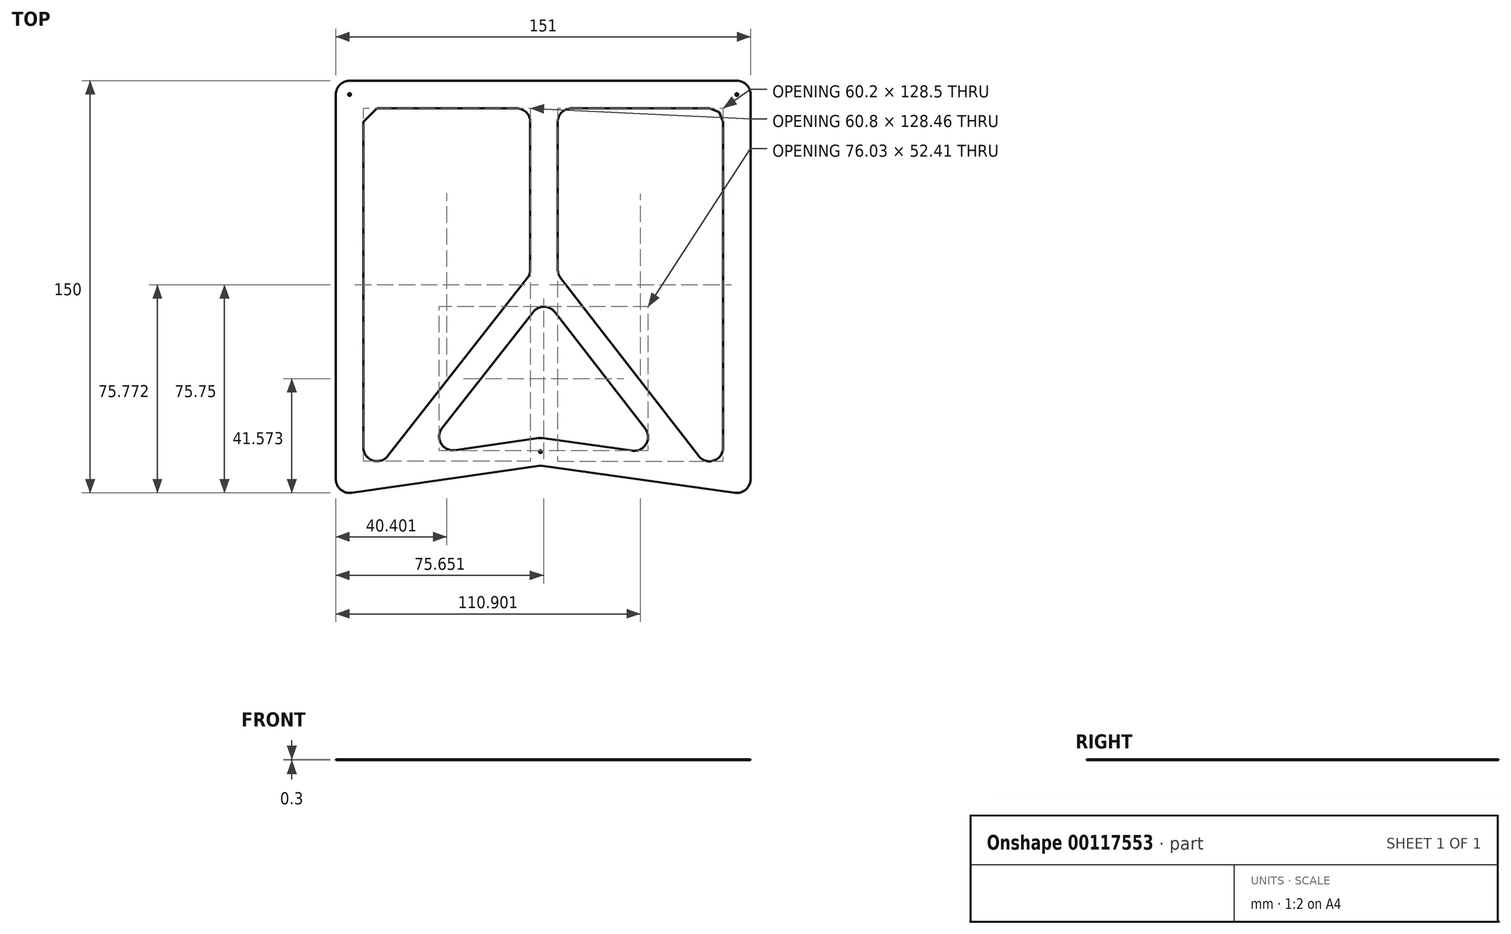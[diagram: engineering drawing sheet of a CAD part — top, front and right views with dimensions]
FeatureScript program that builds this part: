
annotation { "Feature Type Name" : "Feature", "Feature Type Description" : "" }
export const myFeature = defineFeature(function(context is Context, id is Id, definition is map)
    precondition{}
    {
        {
            var Q0;
            Q0=qCreatedBy(makeId("Top.planeOp"),FACE);
            var sketch = newSketch(context, id + "F0", { "sketchPlane" : qUnion([Q0])});
            skLineSegment(sketch, "E0.bottom", {"start": v(-40, 65) * mm, "end": v(40, 65) * mm});
            skLineSegment(sketch, "E0.top", {"start": v(-40, -65) * mm, "end": v(40, -65) * mm});
            skLineSegment(sketch, "E0.left", {"start": v(-40, 65) * mm, "end": v(-40, -65) * mm});
            skLineSegment(sketch, "E0.right", {"start": v(40, 65) * mm, "end": v(40, -65) * mm});
            skLineSegment(sketch, "E1", {"start": v(-40, 0) * mm, "end": v(40, 0) * mm, "construction": true});
            skLineSegment(sketch, "E2.0", {"start": v(-29.6, 64.6) * mm, "end": v(29.6, 64.6) * mm});
            skLineSegment(sketch, "E2.1", {"start": v(-39.6, 54.6) * mm, "end": v(-39.6, -54.6) * mm});
            skLineSegment(sketch, "E2.2", {"start": v(-29.6, -64.6) * mm, "end": v(39.6, -64.6) * mm});
            skLineSegment(sketch, "E2.3", {"start": v(39.6, 54.6) * mm, "end": v(39.6, -64.6) * mm});
            skLineSegment(sketch, "E3.bottom", {"start": v(-15, 25) * mm, "end": v(35, 25) * mm});
            skLineSegment(sketch, "E3.top", {"start": v(-15, -45) * mm, "end": v(35, -45) * mm});
            skLineSegment(sketch, "E3.left", {"start": v(-15, 25) * mm, "end": v(-15, -45) * mm});
            skLineSegment(sketch, "E3.right", {"start": v(35, 25) * mm, "end": v(35, -45) * mm});
            skLineSegment(sketch, "E4.0", {"start": v(-14.6, 24.6) * mm, "end": v(34.6, 24.6) * mm});
            skLineSegment(sketch, "E4.1", {"start": v(-14.6, 24.6) * mm, "end": v(-14.6, -44.6) * mm});
            skLineSegment(sketch, "E4.2", {"start": v(-14.6, -44.6) * mm, "end": v(34.6, -44.6) * mm});
            skLineSegment(sketch, "E4.3", {"start": v(34.6, 24.6) * mm, "end": v(34.6, -44.6) * mm});
            skPoint(sketch, "E5.visualSharp", {"position": v(-39.6, -64.6) * mm});
            skLineSegment(sketch, "E6", {"start": v(29.6, 64.6) * mm, "end": v(34.19, 62.7) * mm});
            skLineSegment(sketch, "E7", {"start": v(39.6, 54.6) * mm, "end": v(37.7, 59.19) * mm});
            skLineSegment(sketch, "E8", {"start": v(29.6, 64.6) * mm, "end": v(39.6, 54.6) * mm, "construction": true});
            skLineSegment(sketch, "E9", {"start": v(39.6, 54.6) * mm, "end": v(39.6, 59.19) * mm, "construction": true});
            skLineSegment(sketch, "E10", {"start": v(39.6, 59.19) * mm, "end": v(37.7, 59.19) * mm, "construction": true});
            skLineSegment(sketch, "E11", {"start": v(37.7, 59.19) * mm, "end": v(36.36, 57.84) * mm, "construction": true});
            skLineSegment(sketch, "E12", {"start": v(-39.6, -54.6) * mm, "end": v(-29.6, -64.6) * mm});
            skLineSegment(sketch, "E13", {"start": v(-39.6, -54.6) * mm, "end": v(-39.6, -64.6) * mm, "construction": true});
            skLineSegment(sketch, "E14", {"start": v(-39.6, -64.6) * mm, "end": v(-29.6, -64.6) * mm, "construction": true});
            skLineSegment(sketch, "E15", {"start": v(-39.6, 54.6) * mm, "end": v(-36.67, 61.67) * mm});
            skLineSegment(sketch, "E16", {"start": v(-36.67, 61.67) * mm, "end": v(-29.6, 64.6) * mm});
            skLineSegment(sketch, "E17", {"start": v(-29.6, 64.6) * mm, "end": v(-39.6, 54.6) * mm, "construction": true});
            skLineSegment(sketch, "E18", {"start": v(-36.67, 64.6) * mm, "end": v(-36.67, 61.67) * mm, "construction": true});
            skLineSegment(sketch, "E19", {"start": v(-36.67, 61.67) * mm, "end": v(-34.6, 59.6) * mm, "construction": true});
            skLineSegment(sketch, "E20", {"start": v(-29.6, 64.6) * mm, "end": v(-39.6, 64.6) * mm, "construction": true});
            skLineSegment(sketch, "E21", {"start": v(-39.6, 64.6) * mm, "end": v(-39.6, 54.6) * mm, "construction": true});
            skLineSegment(sketch, "E22", {"start": v(34.19, 62.7) * mm, "end": v(37.7, 59.19) * mm});
            skSolve(sketch);
        }
        {
            var Q0;
            Q0=qCreatedBy(makeId("Top.planeOp"),FACE);
            var sketch = newSketch(context, id + "F1", { "sketchPlane" : qUnion([Q0])});
            skCircle(sketch, "E23", {"center": v(118.5, 40) * mm, "radius": 0.5 * mm});
            skCircle(sketch, "E24", {"center": v(190, 170) * mm, "radius": 0.5 * mm});
            skCircle(sketch, "E25", {"center": v(49, 170) * mm, "radius": 0.5 * mm});
            skSolve(sketch);
        }
        {
            var Q0;
            Q0 = qSketchRegion(id + "F1", true);
            extrude(context, id + "F2", {"entities" : qUnion([Q0]), "depth" : .3 * mm, "offsetDistance" : 25 * mm});
        }
        {
            var Q0;
            Q0=qCreatedBy(makeId("Top.planeOp"),FACE);
            var sketch = newSketch(context, id + "F3", { "sketchPlane" : qUnion([Q0])});
            skArc(sketch, "E26", {"start": v(119.2, 44.95) * mm, "mid": v(118.5, 45) * mm, "end": v(117.79, 44.95) * mm});
            skArc(sketch, "E27", {"start": v(195, 170) * mm, "mid": v(193.54, 173.54) * mm, "end": v(190, 175) * mm});
            skArc(sketch, "E28", {"start": v(49, 175) * mm, "mid": v(45.46, 173.54) * mm, "end": v(44, 170) * mm});
            skLineSegment(sketch, "E29", {"start": v(44, 170) * mm, "end": v(44, 30) * mm});
            skLineSegment(sketch, "E30", {"start": v(195, 30) * mm, "end": v(195, 170) * mm});
            skLineSegment(sketch, "E31", {"start": v(49, 175) * mm, "end": v(190, 175) * mm});
            skArc(sketch, "E32.filletArc", {"start": v(44, 30) * mm, "mid": v(45.73, 26.22) * mm, "end": v(49.71, 25.05) * mm});
            skArc(sketch, "E33.filletArc", {"start": v(189.3, 25.05) * mm, "mid": v(193.28, 26.23) * mm, "end": v(195, 30) * mm});
            skLineSegment(sketch, "E34.0", {"start": v(59, 165) * mm, "end": v(109.8, 165) * mm});
            skLineSegment(sketch, "E34.1", {"start": v(54, 160) * mm, "end": v(54, 41.54) * mm});
            skLineSegment(sketch, "E34.3", {"start": v(185, 41.5) * mm, "end": v(185, 160) * mm});
            skArc(sketch, "E35.filletArc", {"start": v(59, 165) * mm, "mid": v(55.46, 163.54) * mm, "end": v(54, 160) * mm, "construction": true});
            skArc(sketch, "E36.filletArc", {"start": v(185, 160) * mm, "mid": v(183.54, 163.54) * mm, "end": v(180, 165) * mm, "construction": true});
            skLineSegment(sketch, "E37", {"start": v(87.33, 40.57) * mm, "end": v(117.79, 44.95) * mm});
            skLineSegment(sketch, "E38", {"start": v(151.99, 40.37) * mm, "end": v(119.2, 44.95) * mm});
            skLineSegment(sketch, "E39", {"start": v(49.71, 25.05) * mm, "end": v(118.5, 34.95) * mm});
            skLineSegment(sketch, "E40", {"start": v(189.3, 25.05) * mm, "end": v(118.5, 34.95) * mm});
            skLineSegment(sketch, "E41", {"start": v(82.68, 39.9) * mm, "end": v(84.1, 30) * mm, "construction": true});
            skLineSegment(sketch, "E42", {"start": v(54, 100.77) * mm, "end": v(44, 100.77) * mm, "construction": true});
            skLineSegment(sketch, "E43", {"start": v(49, 25) * mm, "end": v(190, 25) * mm, "construction": true});
            skLineSegment(sketch, "E44.bottom", {"start": v(40, 200) * mm, "end": v(200, 200) * mm, "construction": true});
            skLineSegment(sketch, "E44.top", {"start": v(40, 0) * mm, "end": v(200, 0) * mm, "construction": true});
            skLineSegment(sketch, "E44.left", {"start": v(0, 200) * mm, "end": v(0, 0) * mm, "construction": true});
            skLineSegment(sketch, "E44.right", {"start": v(200, 200) * mm, "end": v(200, 0) * mm, "construction": true});
            skLineSegment(sketch, "E45", {"start": v(40, 200) * mm, "end": v(40, 0) * mm, "construction": true});
            skLineSegment(sketch, "E46", {"start": v(200, 200) * mm, "end": v(240, 200) * mm, "construction": true});
            skLineSegment(sketch, "E47", {"start": v(240, 200) * mm, "end": v(240, 0) * mm, "construction": true});
            skLineSegment(sketch, "E48", {"start": v(240, 0) * mm, "end": v(200, 0) * mm, "construction": true});
            skLineSegment(sketch, "E49", {"start": v(54, 160) * mm, "end": v(59, 165) * mm});
            skLineSegment(sketch, "E50", {"start": v(180, 165) * mm, "end": v(183.54, 163.54) * mm});
            skLineSegment(sketch, "E51", {"start": v(183.54, 163.54) * mm, "end": v(185, 160) * mm});
            skLineSegment(sketch, "E52.0", {"start": v(113.74, 103.21) * mm, "end": v(62.93, 38.46) * mm});
            skLineSegment(sketch, "E52.1", {"start": v(114.8, 160) * mm, "end": v(114.8, 106.3) * mm});
            skLineSegment(sketch, "E53.0", {"start": v(125.85, 103.22) * mm, "end": v(176.05, 38.44) * mm});
            skLineSegment(sketch, "E53.1", {"start": v(124.8, 160) * mm, "end": v(124.8, 106.28) * mm});
            skLineSegment(sketch, "E54.0", {"start": v(123.73, 90.84) * mm, "end": v(156.63, 48.38) * mm});
            skLineSegment(sketch, "E54.1", {"start": v(115.84, 90.87) * mm, "end": v(82.69, 48.6) * mm});
            skArc(sketch, "E55.filletArc", {"start": v(114.8, 160) * mm, "mid": v(113.34, 163.54) * mm, "end": v(109.8, 165) * mm});
            skArc(sketch, "E56.filletArc", {"start": v(54, 41.54) * mm, "mid": v(57.37, 36.82) * mm, "end": v(62.93, 38.46) * mm});
            skArc(sketch, "E57.filletArc", {"start": v(82.69, 48.6) * mm, "mid": v(82.3, 43.01) * mm, "end": v(87.33, 40.57) * mm});
            skArc(sketch, "E58.filletArc", {"start": v(151.99, 40.37) * mm, "mid": v(157, 42.81) * mm, "end": v(156.63, 48.38) * mm});
            skArc(sketch, "E59.filletArc", {"start": v(176.05, 38.44) * mm, "mid": v(181.62, 36.77) * mm, "end": v(185, 41.5) * mm});
            skLineSegment(sketch, "E60", {"start": v(129.8, 165) * mm, "end": v(180, 165) * mm});
            skArc(sketch, "E61.filletArc", {"start": v(129.8, 165) * mm, "mid": v(126.27, 163.54) * mm, "end": v(124.8, 160) * mm});
            skLineSegment(sketch, "E62", {"start": v(114.8, 104.57) * mm, "end": v(124.8, 104.57) * mm, "construction": true});
            skLineSegment(sketch, "E63", {"start": v(119.8, 95.91) * mm, "end": v(114.8, 104.57) * mm, "construction": true});
            skLineSegment(sketch, "E64", {"start": v(119.8, 95.91) * mm, "end": v(124.8, 104.57) * mm, "construction": true});
            skArc(sketch, "E65.filletArc", {"start": v(123.73, 90.84) * mm, "mid": v(119.8, 92.78) * mm, "end": v(115.84, 90.87) * mm});
            skArc(sketch, "E66.filletArc", {"start": v(113.74, 103.21) * mm, "mid": v(114.53, 104.67) * mm, "end": v(114.8, 106.3) * mm});
            skArc(sketch, "E67.filletArc", {"start": v(124.8, 106.28) * mm, "mid": v(125.07, 104.66) * mm, "end": v(125.85, 103.22) * mm});
            skSolve(sketch);
        }
        {
            var Q0;
            Q0 = qSketchRegion(id + "F3", true);
            extrude(context, id + "F4", {"entities" : qUnion([Q0]), "depth" : .3 * mm, "offsetDistance" : 25 * mm});
        }
    });
